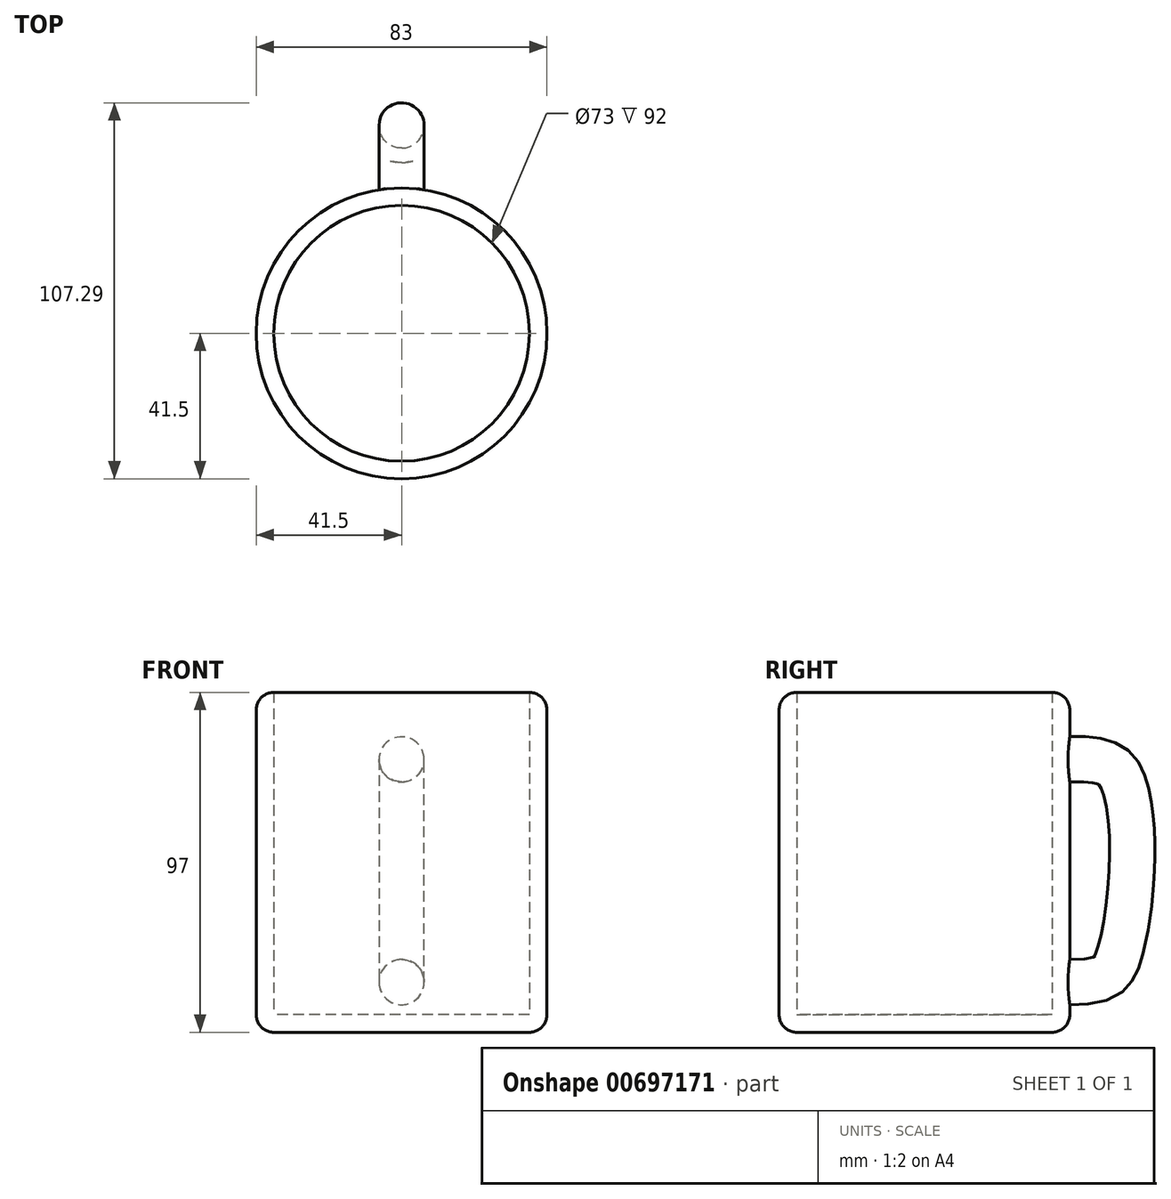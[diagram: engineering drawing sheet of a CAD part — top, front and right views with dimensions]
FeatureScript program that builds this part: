
annotation { "Feature Type Name" : "Feature", "Feature Type Description" : "" }
export const myFeature = defineFeature(function(context is Context, id is Id, definition is map)
    precondition{}
    {
        {
            var Q0;
            Q0=qCreatedBy(makeId("Top.planeOp"),FACE);
            var sketch = newSketch(context, id + "F0", { "sketchPlane" : qUnion([Q0])});
            skCircle(sketch, "E0", {"center": v(0, 0) * mm, "radius": 41.5 * mm});
            skSolve(sketch);
        }
        {
            var Q0;
            Q0 = qSketchRegion(id + "F0", true);
            extrude(context, id + "F1", {"entities" : qUnion([Q0]), "depth" : 97 * mm, "offsetDistance" : 25 * mm});
        }
        {
            var Q0;
            Q0=qCreatedBy(makeId("Right.planeOp"),FACE);
            var sketch = newSketch(context, id + "F2", { "sketchPlane" : qUnion([Q0])});
            skFitSpline(sketch, "E1", {"points": [v(40.86, 82.28) * mm, v(61.37, 71.63) * mm, v(60.69, 23.9) * mm, v(38.73, 10.02) * mm], "startDerivative": vector(131.93, 6.4) * mm, "endDerivative": vector(-159.6, 10.17) * mm});
            skSolve(sketch);
        }
        {
            var Q0;
            Q0=qCreatedBy(makeId("Front.planeOp"),FACE);
            cPlane(context, id + "F3", {"entities" : qUnion([Q0]), "cplaneType" : CPlaneType.OFFSET, "offset" : 41.3 * mm, "oppositeDirection" : true, "width" : 150 * mm, "height" : 150 * mm});
        }
        {
            var Q0;
            Q0=qCreatedBy(id+"F3.planeOp",FACE);
            var sketch = newSketch(context, id + "F4", { "sketchPlane" : qUnion([Q0])});
            skCircle(sketch, "E2", {"center": v(0, 77.88) * mm, "radius": 6.46 * mm});
            skSolve(sketch);
        }
        {
            var Q0;
            Q0 = qSketchRegion(id + "F4", true);
            var Q1;
            Q1 = qConstructionFilter(qBodyType(qCreatedBy(id + "F2" ,EDGE), BodyType.WIRE), ConstructionObject.NO);
            sweep(context, id + "F5", {"operationType" : NewBodyOperationType.ADD, "profiles" : qUnion([Q0]), "path" : qUnion([Q1])});
        }
        {
            var Q0;
            Q0=makeQuery(id+"F1.opExtrude","CAP_FACE",FACE,{"disambiguationData":[OSD([sQuery(id+"F0.wireOp",EDGE,"E0")])],"isStart":false});
            shell(context, id + "F6", {"entities" : qUnion([Q0]), "thickness" : 5 * mm});
        }
        {
            var Q0;
            Q0=makeQuery(id+"F1.opExtrude","CAP_EDGE",EDGE,{"disambiguationData":[OSD([sQuery(id+"F0.wireOp",EDGE,"E0")])],"isStart":false});
            fillet(context, id + "F7", {"entities" : qUnion([Q0]), "radius" : 5 * mm, "tangentPropagation" : true, "allowEdgeOverflow" : false});
        }
        {
            var Q0;
            Q0=makeQuery(id+"F1.opExtrude","CAP_EDGE",EDGE,{"disambiguationData":[OSD([sQuery(id+"F0.wireOp",EDGE,"E0")])],"isStart":true});
            fillet(context, id + "F8", {"entities" : qUnion([Q0]), "radius" : 5 * mm, "tangentPropagation" : true, "allowEdgeOverflow" : false});
        }
    });
